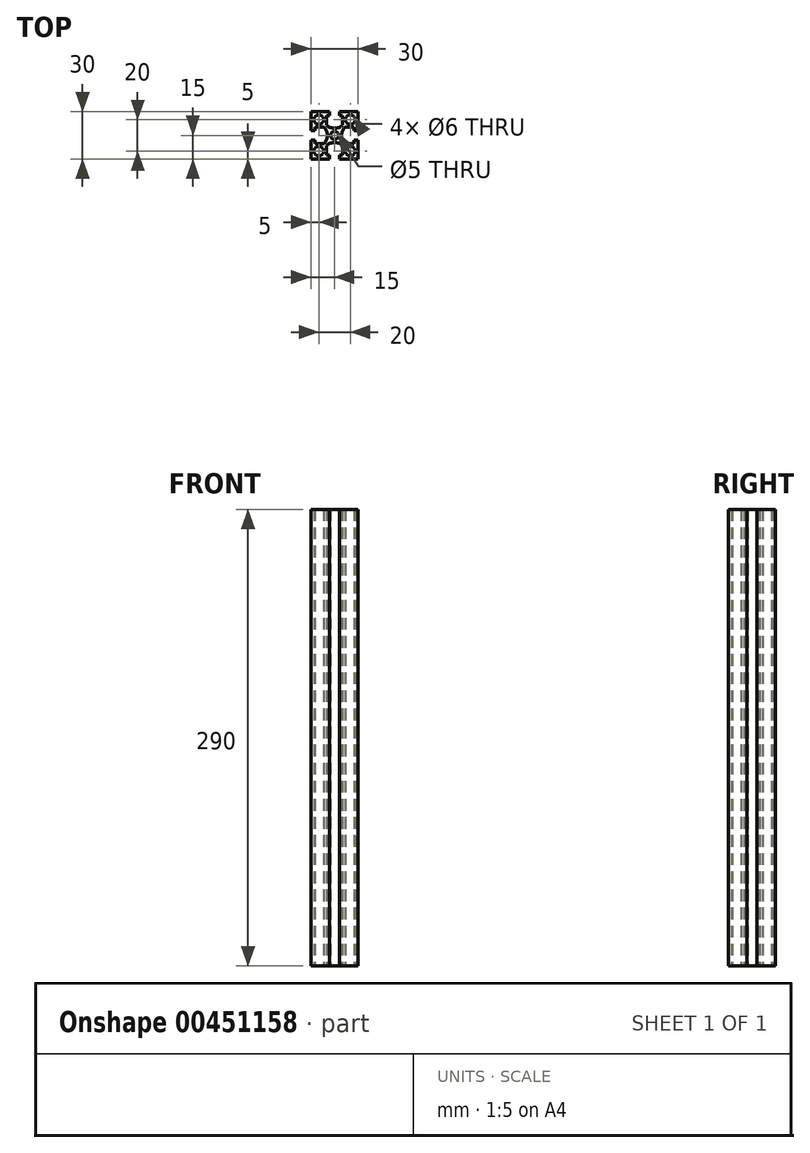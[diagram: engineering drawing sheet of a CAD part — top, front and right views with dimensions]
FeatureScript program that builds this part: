
annotation { "Feature Type Name" : "Feature", "Feature Type Description" : "" }
export const myFeature = defineFeature(function(context is Context, id is Id, definition is map)
    precondition{}
    {
        {
            var Q0;
            Q0=qCreatedBy(makeId("Top.planeOp"),FACE);
            var sketch = newSketch(context, id + "F0", { "sketchPlane" : qUnion([Q0])});
            skCircle(sketch, "E0", {"center": v(-10, 10) * mm, "radius": 3 * mm});
            skCircle(sketch, "E1.MirrorC", {"center": v(-10, -10) * mm, "radius": 3 * mm});
            skLineSegment(sketch, "E2.top", {"start": v(-15, 3.15) * mm, "end": v(-15, -3.15) * mm});
            skLineSegment(sketch, "E2.left", {"start": v(-12.5, 3.15) * mm, "end": v(-15, 3.15) * mm});
            skLineSegment(sketch, "E2.right", {"start": v(-12.5, -3.15) * mm, "end": v(-15, -3.15) * mm});
            skLineSegment(sketch, "E3.bottom", {"start": v(-12.5, 5.15) * mm, "end": v(-12.5, 3.15) * mm});
            skLineSegment(sketch, "E3.left", {"start": v(-12.5, 5.15) * mm, "end": v(-6.55, 5.15) * mm});
            skLineSegment(sketch, "E3.right", {"start": v(-12.5, -5.15) * mm, "end": v(-6.55, -5.15) * mm});
            skArc(sketch, "E4", {"start": v(-6.55, -5.15) * mm, "mid": v(-4.5, 0) * mm, "end": v(-6.55, 5.15) * mm});
            skLineSegment(sketch, "E5.trimOffspring", {"start": v(-12.5, -3.15) * mm, "end": v(-12.5, -5.15) * mm});
            skLineSegment(sketch, "E6.bottom", {"start": v(15, -15) * mm, "end": v(-15, -15) * mm});
            skLineSegment(sketch, "E6.top", {"start": v(15, 15) * mm, "end": v(-15, 15) * mm});
            skLineSegment(sketch, "E6.left", {"start": v(15, -15) * mm, "end": v(15, 15) * mm});
            skLineSegment(sketch, "E6.right", {"start": v(-15, -15) * mm, "end": v(-15, 15) * mm});
            skPoint(sketch, "E6.middle", {"position": v(0, 0) * mm});
            skCircle(sketch, "E7.MirrorC", {"center": v(10, 10) * mm, "radius": 3 * mm});
            skCircle(sketch, "E8.MirrorC", {"center": v(10, -10) * mm, "radius": 3 * mm});
            skLineSegment(sketch, "E9.1.0", {"start": v(-5.15, -12.5) * mm, "end": v(-3.15, -12.5) * mm});
            skArc(sketch, "E9.1.1", {"start": v(5.15, -6.55) * mm, "mid": v(0, -4.5) * mm, "end": v(-5.15, -6.55) * mm});
            skLineSegment(sketch, "E9.1.2", {"start": v(-3.15, -15) * mm, "end": v(3.15, -15) * mm});
            skLineSegment(sketch, "E9.1.3", {"start": v(-3.15, -12.5) * mm, "end": v(-3.15, -15) * mm});
            skLineSegment(sketch, "E9.1.4", {"start": v(-5.15, -12.5) * mm, "end": v(-5.15, -6.55) * mm});
            skLineSegment(sketch, "E9.1.5", {"start": v(3.15, -12.5) * mm, "end": v(5.15, -12.5) * mm});
            skLineSegment(sketch, "E9.1.6", {"start": v(5.15, -12.5) * mm, "end": v(5.15, -6.55) * mm});
            skLineSegment(sketch, "E9.1.7", {"start": v(3.15, -12.5) * mm, "end": v(3.15, -15) * mm});
            skLineSegment(sketch, "E9.2.0", {"start": v(12.5, -5.15) * mm, "end": v(12.5, -3.15) * mm});
            skArc(sketch, "E9.2.1", {"start": v(6.55, 5.15) * mm, "mid": v(4.5, 0) * mm, "end": v(6.55, -5.15) * mm});
            skLineSegment(sketch, "E9.2.2", {"start": v(15, -3.15) * mm, "end": v(15, 3.15) * mm});
            skLineSegment(sketch, "E9.2.3", {"start": v(12.5, -3.15) * mm, "end": v(15, -3.15) * mm});
            skLineSegment(sketch, "E9.2.4", {"start": v(12.5, -5.15) * mm, "end": v(6.55, -5.15) * mm});
            skLineSegment(sketch, "E9.2.5", {"start": v(12.5, 3.15) * mm, "end": v(12.5, 5.15) * mm});
            skLineSegment(sketch, "E9.2.6", {"start": v(12.5, 5.15) * mm, "end": v(6.55, 5.15) * mm});
            skLineSegment(sketch, "E9.2.7", {"start": v(12.5, 3.15) * mm, "end": v(15, 3.15) * mm});
            skLineSegment(sketch, "E9.3.0", {"start": v(5.15, 12.5) * mm, "end": v(3.15, 12.5) * mm});
            skArc(sketch, "E9.3.1", {"start": v(-5.15, 6.55) * mm, "mid": v(0, 4.5) * mm, "end": v(5.15, 6.55) * mm});
            skLineSegment(sketch, "E9.3.2", {"start": v(3.15, 15) * mm, "end": v(-3.15, 15) * mm});
            skLineSegment(sketch, "E9.3.3", {"start": v(3.15, 12.5) * mm, "end": v(3.15, 15) * mm});
            skLineSegment(sketch, "E9.3.4", {"start": v(5.15, 12.5) * mm, "end": v(5.15, 6.55) * mm});
            skLineSegment(sketch, "E9.3.5", {"start": v(-3.15, 12.5) * mm, "end": v(-5.15, 12.5) * mm});
            skLineSegment(sketch, "E9.3.6", {"start": v(-5.15, 12.5) * mm, "end": v(-5.15, 6.55) * mm});
            skLineSegment(sketch, "E9.3.7", {"start": v(-3.15, 12.5) * mm, "end": v(-3.15, 15) * mm});
            skCircle(sketch, "E10", {"center": v(0, 0) * mm, "radius": 2.5 * mm});
            skSolve(sketch);
        }
        {
            var Q0;
            Q0=makeQuery(id+"F0.imprint","IMPRINT",FACE,{"disambiguationData":[TD([[makeQuery(id+"F0.imprint","IMPRINT",EDGE,{"derivedFrom":sQuery(id+"F0.wireOp",EDGE,"E0")}),-1.0]])]});
            extrude(context, id + "F1", {"entities" : qUnion([Q0]), "depth" : 290 * mm, "offsetDistance" : 25 * mm});
        }
    });
